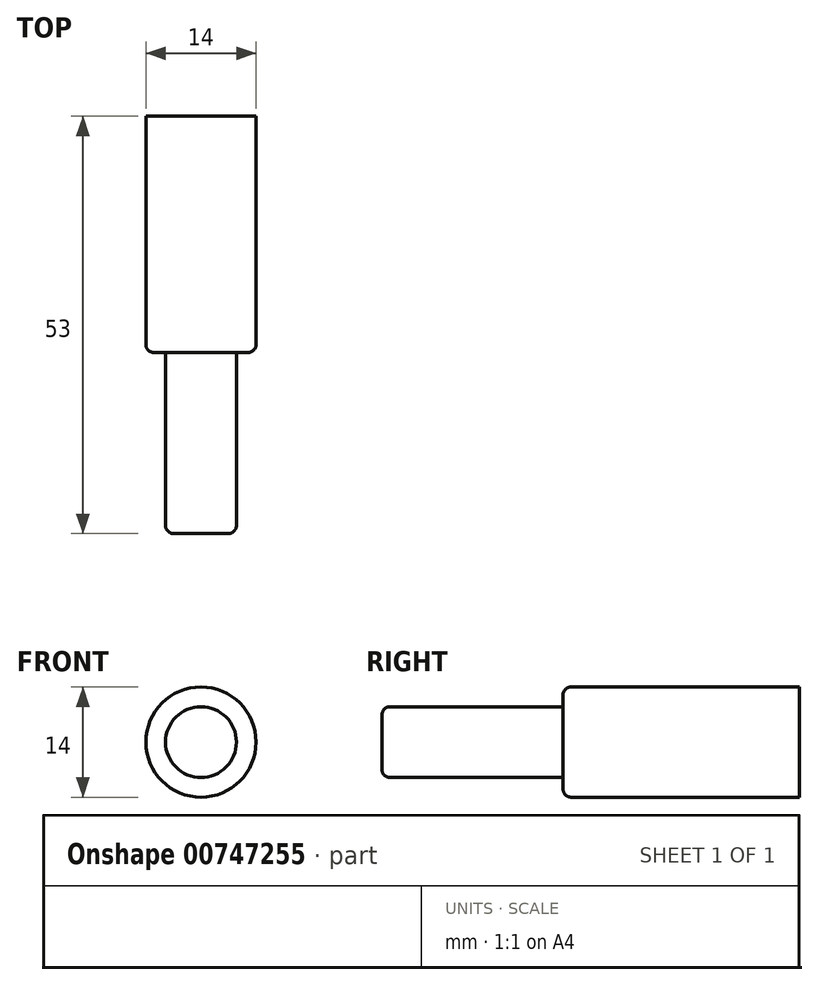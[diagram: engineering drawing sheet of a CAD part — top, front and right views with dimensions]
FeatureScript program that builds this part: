
annotation { "Feature Type Name" : "Feature", "Feature Type Description" : "" }
export const myFeature = defineFeature(function(context is Context, id is Id, definition is map)
    precondition{}
    {
        {
            var Q0;
            Q0=qCreatedBy(makeId("Front.planeOp"),FACE);
            var sketch = newSketch(context, id + "F0", { "sketchPlane" : qUnion([Q0])});
            skCircle(sketch, "E0", {"center": v(0, 0) * mm, "radius": 7 * mm});
            skCircle(sketch, "E1", {"center": v(0, 0) * mm, "radius": 4.5 * mm});
            skSolve(sketch);
        }
        {
            var Q0;
            Q0 = qSketchRegion(id + "F0", true);
            var Q1;
            Q1=makeQuery(id+"F0.imprint","IMPRINT",FACE,{"disambiguationData":[TD([[makeQuery(id+"F0.imprint","IMPRINT",EDGE,{"derivedFrom":sQuery(id+"F0.wireOp",EDGE,"E1")}),1.0]])]});
            extrude(context, id + "F1", {"entities" : qUnion([Q0, Q1]), "oppositeDirection" : true, "depth" : 30 * mm, "offsetDistance" : 25 * mm});
        }
        {
            var Q0;
            Q0=makeQuery(id+"F0.imprint","IMPRINT",FACE,{"disambiguationData":[TD([[makeQuery(id+"F0.imprint","IMPRINT",EDGE,{"derivedFrom":sQuery(id+"F0.wireOp",EDGE,"E1")}),1.0]])]});
            extrude(context, id + "F2", {"entities" : qUnion([Q0]), "operationType" : NewBodyOperationType.ADD, "depth" : 23 * mm, "offsetDistance" : 25 * mm});
        }
        {
            var Q0;
            Q0=makeQuery(id+"F2.opExtrude","CAP_EDGE",EDGE,{"disambiguationData":[OSD([sQuery(id+"F0.wireOp",EDGE,"E1")])],"isStart":false});
            var Q1;
            Q1=makeQuery(id+"F1.opExtrude","CAP_EDGE",EDGE,{"disambiguationData":[OSD([sQuery(id+"F0.wireOp",EDGE,"E0")])],"isStart":true});
            fillet(context, id + "F3", {"entities" : qUnion([Q0, Q1]), "radius" : 1 * mm, "tangentPropagation" : true, "allowEdgeOverflow" : false});
        }
    });
